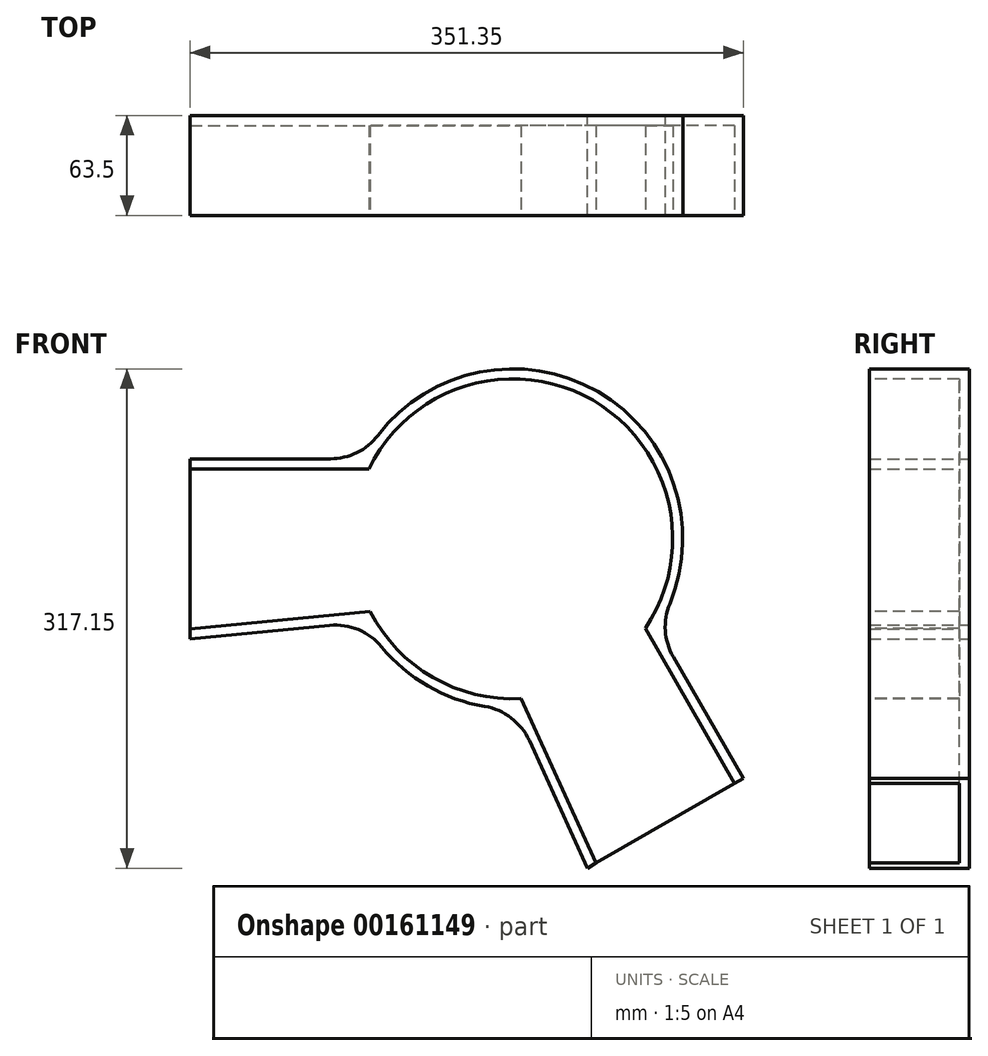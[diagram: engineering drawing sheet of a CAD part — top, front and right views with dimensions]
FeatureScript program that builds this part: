
annotation { "Feature Type Name" : "Feature", "Feature Type Description" : "" }
export const myFeature = defineFeature(function(context is Context, id is Id, definition is map)
    precondition{}
    {
        {
            var Q0;
            Q0=qCreatedBy(makeId("Front.planeOp"),FACE);
            var sketch = newSketch(context, id + "F0", { "sketchPlane" : qUnion([Q0])});
            skLineSegment(sketch, "E0.bottom", {"start": v(0, 0) * mm, "end": v(412.75, 0) * mm, "construction": true});
            skLineSegment(sketch, "E0.top", {"start": v(0, 25.4) * mm, "end": v(412.75, 25.4) * mm, "construction": true});
            skLineSegment(sketch, "E0.left", {"start": v(0, 0) * mm, "end": v(0, 25.4) * mm});
            skLineSegment(sketch, "E0.right", {"start": v(412.75, 0) * mm, "end": v(412.75, 25.4) * mm, "construction": true});
            skLineSegment(sketch, "E1.bottom", {"start": v(304.8, 25.4) * mm, "end": v(663.1, 25.4) * mm, "construction": true});
            skLineSegment(sketch, "E2", {"start": v(304.8, 57.15) * mm, "end": v(304.8, -57.15) * mm});
            skLineSegment(sketch, "E3", {"start": v(304.8, 57.15) * mm, "end": v(393.82, 57.15) * mm});
            skLineSegment(sketch, "E4", {"start": v(611.63, -68.6) * mm, "end": v(656.15, -145.7) * mm});
            skLineSegment(sketch, "E5", {"start": v(656.15, -145.7) * mm, "end": v(557.16, -202.85) * mm});
            skPoint(sketch, "E6.orphan", {"position": v(656.15, -164.27) * mm});
            skLineSegment(sketch, "E7", {"start": v(393.4, -48.66) * mm, "end": v(304.8, -57.15) * mm});
            skLineSegment(sketch, "E8", {"start": v(557.16, -202.85) * mm, "end": v(520.2, -121.87) * mm});
            skLineSegment(sketch, "E9", {"start": v(520.7, 25.4) * mm, "end": v(709.43, -301.48) * mm, "construction": true});
            skPoint(sketch, "E10.endSnap0", {"position": v(206.38, 25.4) * mm});
            skArc(sketch, "E11", {"start": v(609.43, -34.97) * mm, "mid": v(606.61, -52.04) * mm, "end": v(611.63, -68.6) * mm});
            skArc(sketch, "E12", {"start": v(393.82, 57.15) * mm, "mid": v(410.68, 61.08) * mm, "end": v(424.05, 72.06) * mm});
            skLineSegment(sketch, "E13", {"start": v(275.97, 50.8) * mm, "end": v(634.2, 50.8) * mm, "construction": true});
            skLineSegment(sketch, "E14", {"start": v(668.97, -180.62) * mm, "end": v(535.36, 50.8) * mm, "construction": true});
            skLineSegment(sketch, "E15", {"start": v(518.04, 198.6) * mm, "end": v(417.6, 24.64) * mm, "construction": true});
            skLineSegment(sketch, "E16", {"start": v(676.43, 117.33) * mm, "end": v(571.23, -64.88) * mm, "construction": true});
            skLineSegment(sketch, "E17", {"start": v(432.71, 50.8) * mm, "end": v(586.7, -38.1) * mm});
            skLineSegment(sketch, "E18", {"start": v(509.7, 6.35) * mm, "end": v(574.81, 119.12) * mm});
            skCircle(sketch, "E19", {"center": v(509.7, 6.35) * mm, "radius": 88.9 * mm, "construction": true});
            skArc(sketch, "E20", {"start": v(426.43, -62.34) * mm, "mid": v(455.73, -87.14) * mm, "end": v(491.85, -100.11) * mm});
            skArc(sketch, "E21", {"start": v(520.2, -121.87) * mm, "mid": v(508.74, -107.46) * mm, "end": v(491.85, -100.11) * mm});
            skArc(sketch, "E22.converted", {"start": v(426.43, -62.34) * mm, "mid": v(411.62, -51.39) * mm, "end": v(393.4, -48.66) * mm});
            skArc(sketch, "E23.trimOffspring", {"start": v(609.43, -34.97) * mm, "mid": v(563.68, 99.84) * mm, "end": v(424.05, 72.06) * mm});
            skSolve(sketch);
        }
        {
            var Q0;
            Q0=makeQuery(id+"F0.imprint","IMPRINT",FACE,{"disambiguationData":[TD([[makeQuery(id+"F0.imprint","IMPRINT",EDGE,{"derivedFrom":sQuery(id+"F0.wireOp",EDGE,"E2")}),1.0]])]});
            extrude(context, id + "F1", {"entities" : qUnion([Q0]), "depth" : 63.5 * mm});
        }
        {
            var Q0;
            Q0=makeQuery(id+"F1.opExtrude","CAP_FACE",FACE,{"disambiguationData":[OSD([sQuery(id+"F0.wireOp",EDGE,"E2"),sQuery(id+"F0.wireOp",EDGE,"E3"),sQuery(id+"F0.wireOp",EDGE,"E4"),sQuery(id+"F0.wireOp",EDGE,"E5"),sQuery(id+"F0.wireOp",EDGE,"E7"),sQuery(id+"F0.wireOp",EDGE,"E8"),sQuery(id+"F0.wireOp",EDGE,"E11"),sQuery(id+"F0.wireOp",EDGE,"E12"),sQuery(id+"F0.wireOp",EDGE,"E20"),sQuery(id+"F0.wireOp",EDGE,"E21"),sQuery(id+"F0.wireOp",EDGE,"E22.converted"),sQuery(id+"F0.wireOp",EDGE,"E23.trimOffspring")])],"isStart":false});
            var sketch = newSketch(context, id + "F2", { "sketchPlane" : qUnion([Q0])});
            skArc(sketch, "E24", {"start": v(419.2, -39.81) * mm, "mid": v(458.9, -81.64) * mm, "end": v(514.98, -95.11) * mm});
            skLineSegment(sketch, "E25", {"start": v(288.12, 50.8) * mm, "end": v(418.34, 50.8) * mm});
            skLineSegment(sketch, "E26", {"start": v(293.53, -51.85) * mm, "end": v(419.2, -39.81) * mm});
            skLineSegment(sketch, "E27", {"start": v(656.15, -158.4) * mm, "end": v(593.88, -50.55) * mm});
            skLineSegment(sketch, "E28", {"start": v(570.31, -216.38) * mm, "end": v(514.98, -95.11) * mm});
            skLineSegment(sketch, "E29", {"start": v(293.53, -51.85) * mm, "end": v(288.12, 50.8) * mm});
            skLineSegment(sketch, "E30", {"start": v(570.31, -216.38) * mm, "end": v(656.15, -158.4) * mm});
            skArc(sketch, "E31.trimOffspring", {"start": v(593.88, -50.55) * mm, "mid": v(560.5, 94.34) * mm, "end": v(418.34, 50.8) * mm});
            skSolve(sketch);
        }
        {
            var Q0;
            Q0=qSketchRegion(id+"F2",true);
            extrude(context, id + "F3", {"entities" : qUnion([Q0]), "oppositeDirection" : true, "depth" : 57.15 * mm});
        }
        {
            var Q0;
            Q0=makeQuery(id+"F3.opExtrude","SWEPT_BODY",BODY,{"disambiguationData":[OSD([sQuery(id+"F2.wireOp",EDGE,"E24"),sQuery(id+"F2.wireOp",EDGE,"E25"),sQuery(id+"F2.wireOp",EDGE,"E26"),sQuery(id+"F2.wireOp",EDGE,"E27"),sQuery(id+"F2.wireOp",EDGE,"E28"),sQuery(id+"F2.wireOp",EDGE,"E29"),sQuery(id+"F2.wireOp",EDGE,"E30"),sQuery(id+"F2.wireOp",EDGE,"E31.trimOffspring")])]});
            var Q1;
            Q1=makeQuery(id+"F1.opExtrude","SWEPT_BODY",BODY,{"disambiguationData":[OSD([sQuery(id+"F0.wireOp",EDGE,"E2"),sQuery(id+"F0.wireOp",EDGE,"E3"),sQuery(id+"F0.wireOp",EDGE,"E4"),sQuery(id+"F0.wireOp",EDGE,"E5"),sQuery(id+"F0.wireOp",EDGE,"E7"),sQuery(id+"F0.wireOp",EDGE,"E8"),sQuery(id+"F0.wireOp",EDGE,"E11"),sQuery(id+"F0.wireOp",EDGE,"E12"),sQuery(id+"F0.wireOp",EDGE,"E20"),sQuery(id+"F0.wireOp",EDGE,"E21"),sQuery(id+"F0.wireOp",EDGE,"E22.converted"),sQuery(id+"F0.wireOp",EDGE,"E23.trimOffspring")])]});
            booleanBodies(context, id + "F4", {"operationType" : BooleanOperationType.SUBTRACTION, "tools" : qUnion([Q0]), "targets" : qUnion([Q1])});
        }
    });
